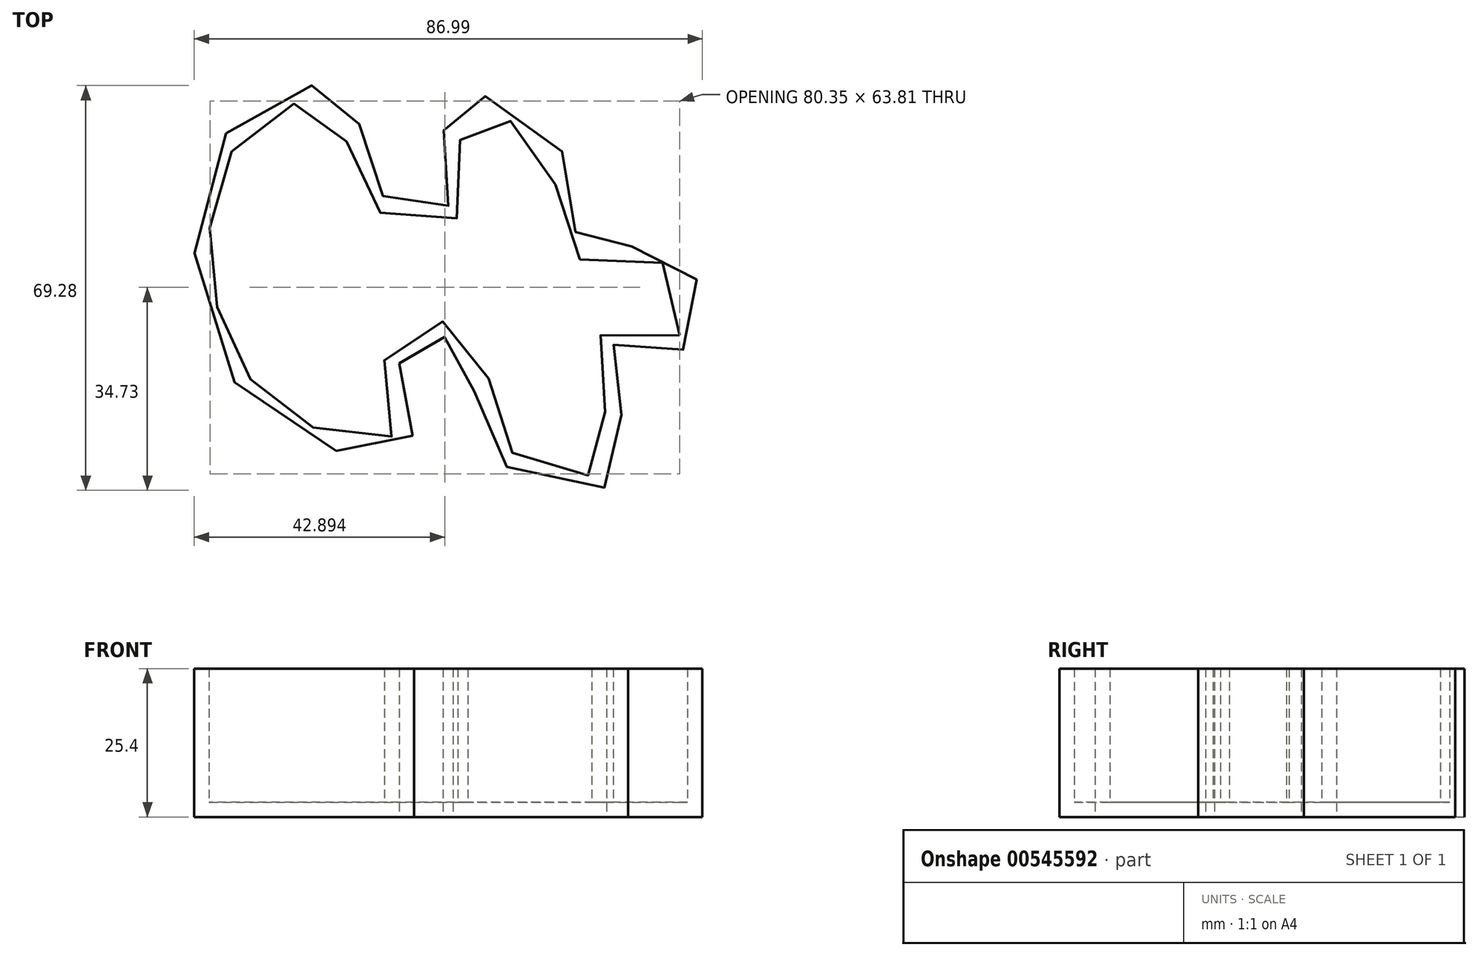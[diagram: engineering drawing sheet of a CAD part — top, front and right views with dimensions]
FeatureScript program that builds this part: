
annotation { "Feature Type Name" : "Feature", "Feature Type Description" : "" }
export const myFeature = defineFeature(function(context is Context, id is Id, definition is map)
    precondition{}
    {
        {
            var Q0;
            Q0=qCreatedBy(makeId("Top.planeOp"),FACE);
            var sketch = newSketch(context, id + "F0", { "sketchPlane" : qUnion([Q0])});
            skFitSpline(sketch, "E0", {"points": [v(-51.24, 36.75) * mm, v(-45.98, -10.39) * mm, v(-19.46, -15.29) * mm, v(-21.24, 0) * mm, v(-10.46, 0) * mm, v(-6.35, -17.47) * mm, v(16.87, -21.49) * mm, v(14.27, 0) * mm, v(27.64, 0) * mm, v(26.25, 15.98) * mm, v(9.92, 17.7) * mm, v(5.35, 35.28) * mm, v(-13.43, 41.85) * mm, v(-12.94, 24.71) * mm, v(-25.53, 27.2) * mm, v(-30.54, 43.13) * mm, v(-51.24, 36.75) * mm]});
            skSolve(sketch);
        }
        {
            var Q0;
            Q0 = qSketchRegion(id + "F0", true);
            extrude(context, id + "F1", {"entities" : qUnion([Q0]), "depth" : 25.4 * mm, "offsetDistance" : 25.4 * mm});
        }
        {
            var Q0;
            Q0=makeQuery(id+"F1.opExtrude","CAP_FACE",FACE,{"disambiguationData":[OSD([sQuery(id+"F0.wireOp",EDGE,"E0")])],"isStart":false});
            shell(context, id + "F2", {"entities" : qUnion([Q0]), "thickness" : 2.54 * mm});
        }
    });
